# Revit family: Pipefitting_IBP_Conex_MaxiPro_StraightCoupler_MP5270
name_source: partatom
category: Pipe Fittings
units: mm (PartAtom-declared; Revit-internal decimal feet)

## family parameters
Always vertical = No
Cut with Voids When Loaded = No
OmniClass Number = 23.65.00.00
OmniClass Title = Supply and Distribution of Liquids and Gases
Part Type = Union
Round Connector Dimension = Use Diameter
Shared = No
Work Plane-Based = No

## types (8) — shared parameters
Application = Air conditioning & refrigeration
Assembly Code = D20
AssetType = Fixed
BIMObjectName = PipeFitting_IBP_Conex_MaxiPro_Straightcoupler_MP5270
ClassificationName = Uniclass2015
ClassificationValue = Pr_65_52_63_18
Description = Straight Press Coupler
ExpectedServiceLifeYears = 25
FittingType = Straight Press Coupler
FluidTemperatureMax = 121 °C
FluidTemperatureMin = -40 °C
IfcExportAs = IfcPipeFitting
IfcExportType = IfcPipeFittingType
Keynote = S
Manufacturer = Conex Banninger
ManufacturerName = IBP
Material = Copper, C12200
MaterialType = Refrigerant Grade Copper, C12200
MaxHydrostaticPressure = 48 bar
NBSDescription = Copper pipeline fittings
NBSObjectName = IBP - Copper pipeline fittings
NBSReference = 90-10-65/315
ORingTemperatureRange = -40°C to 140°C
PipeConnectorType = Press x Press
PressJawCompatability = MaxiPro Jaws supplied by Rothenberger
SealType = HNBR
Shape = Cylindrical
SurfaceFinish = Natural
URL = http://www.conexbanninger.com
WarrantyDescription = Product Guarantee
WarrantyDurationMonths = 60
Weight = 0.00 kg
_BimstoreBibleVersion = 14
_CurrentRevision = 1
_DistributedBy = www.bimmepaus.com.au/
zero-valued in all types: NominalDepth, NominalHeight, NominalLength, _BimSpecGuid

## per-type parameters (varying)
| type | A_Length | B_TubeStopPosition | BeadDepth_Formula | Bead_Dia | ID_DN | L2_BeadDepth | Model | ModelNumber | ModelReference | OD_Formula | ProductCode | S_WallThickness | Size | Type Comments |
| MP5270 0020000 1/4" | 39 mm  [stored 0.127953 ft] | 3 mm  [stored 0.00984252 ft] | 24 mm  [stored 0.0787402 ft] | 2 mm  [stored 0.00656168 ft] | 6 mm  [stored 0.019685 ft] | 8 mm  [stored 0.0262467 ft] | MP5270 0020000 | MP5270 0020000 | 1/4" Connection | 9 mm  [stored 0.0295276 ft] | MP5270 0020000 | 1 mm  [stored 0.00328084 ft] | 1/4" Connection | 1/4" Connection |
| MP5270 0030000 3/8" | 39 mm  [stored 0.127953 ft] | 3 mm  [stored 0.00984252 ft] | 25 mm  [stored 0.082021 ft] | 2 mm  [stored 0.00656168 ft] | 10 mm  [stored 0.0328084 ft] | 7 mm  [stored 0.0229659 ft] | MP5270 0030000 | MP5270 0030000 | 3/8" Connection | 12 mm  [stored 0.0393701 ft] | MP5270 0030000 | 1 mm  [stored 0.00328084 ft] | 3/8" Connection | 3/8" Connection |
| MP5270 0040000 1/2" | 40 mm | 5 mm  [stored 0.0164042 ft] | 26 mm | 3 mm  [stored 0.00984252 ft] | 13 mm | 7 mm  [stored 0.0229659 ft] | MP5270 0040000 | MP5270 0040000 | 1/2" Connection | 16 mm | MP5270 0040000 | 1 mm  [stored 0.00328084 ft] | 1/2" Connection | 1/2" Connection |
| MP5270 0050000 5/8" | 45 mm | 3 mm  [stored 0.00984252 ft] | 29 mm | 3 mm  [stored 0.00984252 ft] | 16 mm | 8 mm  [stored 0.0262467 ft] | MP5270 0050000 | MP5270 0050000 | 5/8" Connection | 19 mm | MP5270 0050000 | 2 mm  [stored 0.00656168 ft] | 5/8" Connection | 5/8" Connection |
| MP5270 0060000 3/4" | 47 mm | 2 mm  [stored 0.00656168 ft] | 27 mm | 3 mm  [stored 0.00984252 ft] | 19 mm | 10 mm  [stored 0.0328084 ft] | MP5270 0060000 | MP5270 0060000 | 3/4" Connection | 22 mm | MP5270 0060000 | 2 mm  [stored 0.00656168 ft] | 3/4" Connection | 3/4" Connection |
| MP5270 0070000 7/8" | 58 mm | 9 mm  [stored 0.0295276 ft] | 38 mm | 3 mm  [stored 0.00984252 ft] | 22 mm | 10 mm  [stored 0.0328084 ft] | MP5270 0070000 | MP5270 0070000 | 7/8" Connection | 26 mm | MP5270 0070000 | 2 mm  [stored 0.00656168 ft] | 7/8" Connection | 7/8" Connection |
| MP5270 0080000 1" | 50 mm | 2 mm  [stored 0.00656168 ft] | 30 mm | 3 mm  [stored 0.00984252 ft] | 26 mm | 10 mm  [stored 0.0328084 ft] | MP5270 0080000 | MP5270 0080000 | 1" Connection | 29 mm | MP5270 0080000 | 2 mm  [stored 0.00656168 ft] | 1" Connection | 1" Connection |
| MP5270 0090000 1 1/8" | 58 mm | 6 mm  [stored 0.019685 ft] | 38 mm | 3 mm  [stored 0.00984252 ft] | 29 mm | 10 mm  [stored 0.0328084 ft] | MP5270 0090000 | MP5270 0090000 | 1 1/8" Connection | 32 mm | MP5270 0090000 | 2 mm  [stored 0.00656168 ft] | 1 1/8" Connection | 1 1/8" Connection |

note: [stored X ft] marks values corroborated as IEEE doubles in the binary element streams (Revit-internal decimal feet)

## geometry (parser evidence)
native form markers: Sweep x4
no freeform markers — native parametric forms only
